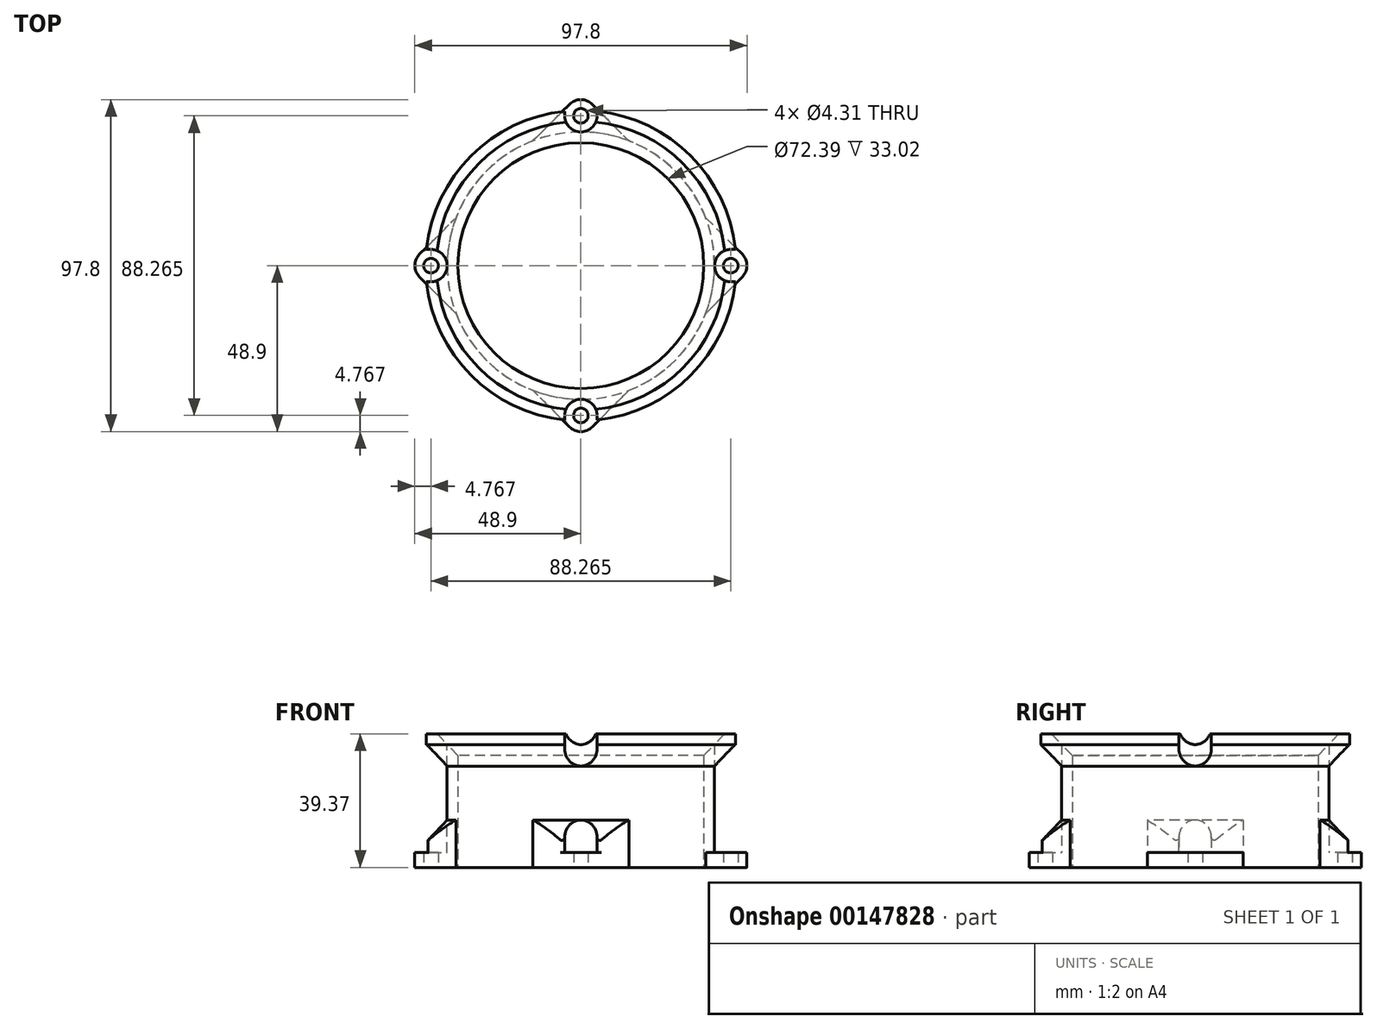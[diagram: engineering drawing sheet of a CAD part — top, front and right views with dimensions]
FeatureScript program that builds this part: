
annotation { "Feature Type Name" : "Feature", "Feature Type Description" : "" }
export const myFeature = defineFeature(function(context is Context, id is Id, definition is map)
    precondition{}
    {
        {
            var Q0;
            Q0=qCreatedBy(makeId("Top.planeOp"),FACE);
            var sketch = newSketch(context, id + "F0", { "sketchPlane" : qUnion([Q0])});
            skCircle(sketch, "E0", {"center": v(0, 0) * mm, "radius": 36.2 * mm});
            skLineSegment(sketch, "E1", {"start": v(-44.13, 0) * mm, "end": v(44.13, 0) * mm, "construction": true});
            skLineSegment(sketch, "E2", {"start": v(0, 44.13) * mm, "end": v(0, -44.13) * mm, "construction": true});
            skArc(sketch, "E3", {"start": v(3.37, 47.5) * mm, "mid": v(0, 48.9) * mm, "end": v(-3.37, 47.5) * mm});
            skLineSegment(sketch, "E4", {"start": v(3.37, 47.5) * mm, "end": v(14.11, 36.75) * mm});
            skArc(sketch, "E5", {"start": v(36.75, 14.11) * mm, "mid": v(27.84, 27.84) * mm, "end": v(14.11, 36.75) * mm});
            skLineSegment(sketch, "E6", {"start": v(-3.37, 47.5) * mm, "end": v(-14.11, 36.75) * mm});
            skArc(sketch, "E7", {"start": v(-47.5, 3.37) * mm, "mid": v(-48.9, 0) * mm, "end": v(-47.5, -3.37) * mm});
            skArc(sketch, "E8", {"start": v(-14.11, 36.75) * mm, "mid": v(-27.84, 27.84) * mm, "end": v(-36.75, 14.11) * mm});
            skArc(sketch, "E9", {"start": v(47.5, -3.37) * mm, "mid": v(48.9, 0) * mm, "end": v(47.5, 3.37) * mm});
            skArc(sketch, "E10", {"start": v(-3.37, -47.5) * mm, "mid": v(0, -48.9) * mm, "end": v(3.37, -47.5) * mm});
            skLineSegment(sketch, "E11", {"start": v(36.75, 14.11) * mm, "end": v(47.5, 3.37) * mm});
            skLineSegment(sketch, "E12", {"start": v(47.5, -3.37) * mm, "end": v(36.75, -14.11) * mm});
            skLineSegment(sketch, "E13", {"start": v(-3.37, -47.5) * mm, "end": v(-14.11, -36.75) * mm});
            skLineSegment(sketch, "E14", {"start": v(3.37, -47.5) * mm, "end": v(14.11, -36.75) * mm});
            skLineSegment(sketch, "E15", {"start": v(-6.74, 44.13) * mm, "end": v(6.74, 44.13) * mm, "construction": true});
            skLineSegment(sketch, "E16", {"start": v(-6.74, -44.13) * mm, "end": v(6.74, -44.13) * mm, "construction": true});
            skLineSegment(sketch, "E17", {"start": v(-47.5, 3.37) * mm, "end": v(-36.75, 14.11) * mm});
            skLineSegment(sketch, "E18", {"start": v(-47.5, -3.37) * mm, "end": v(-36.75, -14.11) * mm});
            skLineSegment(sketch, "E19", {"start": v(44.13, 6.74) * mm, "end": v(44.13, -6.74) * mm, "construction": true});
            skLineSegment(sketch, "E20", {"start": v(-44.13, 6.74) * mm, "end": v(-44.13, -6.74) * mm, "construction": true});
            skArc(sketch, "E21", {"start": v(-36.75, -14.11) * mm, "mid": v(-27.84, -27.84) * mm, "end": v(-14.11, -36.75) * mm});
            skArc(sketch, "E22", {"start": v(14.11, -36.75) * mm, "mid": v(27.84, -27.84) * mm, "end": v(36.75, -14.11) * mm});
            skSolve(sketch);
        }
        {
            var Q0;
            Q0=qSketchRegion(id+"F0",true);
            extrude(context, id + "F1", {"entities" : qUnion([Q0]), "depth" : 4.44 * mm});
        }
        {
            var Q0;
            Q0=makeQuery(id+"F1.opExtrude","CAP_FACE",FACE,{"disambiguationData":[OSD([sQuery(id+"F0.wireOp",EDGE,"E0"),sQuery(id+"F0.wireOp",EDGE,"E3"),sQuery(id+"F0.wireOp",EDGE,"E4"),sQuery(id+"F0.wireOp",EDGE,"E5"),sQuery(id+"F0.wireOp",EDGE,"E6"),sQuery(id+"F0.wireOp",EDGE,"E7"),sQuery(id+"F0.wireOp",EDGE,"E8"),sQuery(id+"F0.wireOp",EDGE,"E9"),sQuery(id+"F0.wireOp",EDGE,"E10"),sQuery(id+"F0.wireOp",EDGE,"E11"),sQuery(id+"F0.wireOp",EDGE,"E12"),sQuery(id+"F0.wireOp",EDGE,"E13"),sQuery(id+"F0.wireOp",EDGE,"E14"),sQuery(id+"F0.wireOp",EDGE,"E17"),sQuery(id+"F0.wireOp",EDGE,"E18"),sQuery(id+"F0.wireOp",EDGE,"E21"),sQuery(id+"F0.wireOp",EDGE,"E22")])],"isStart":false});
            var sketch = newSketch(context, id + "F2", { "sketchPlane" : qUnion([Q0])});
            skCircle(sketch, "E23", {"center": v(0, 0) * mm, "radius": 39.37 * mm});
            skCircle(sketch, "E24", {"center": v(0, 0) * mm, "radius": 36.2 * mm});
            skSolve(sketch);
        }
        {
            var Q0;
            Q0=qSketchRegion(id+"F2",true);
            extrude(context, id + "F3", {"entities" : qUnion([Q0]), "operationType" : NewBodyOperationType.ADD, "depth" : 25.4 * mm});
        }
        {
            var Q0;
            {var subQ3=sQuery(id+"F2.wireOp",EDGE,"E23");var subQ4=sQuery(id+"F0.wireOp",EDGE,"E4");Q0=makeQuery(id+"F3.boolean.opBoolean","SPLIT",EDGE,{"disambiguationData":[TD([makeQuery(id+"F1.opExtrude","SWEPT_FACE",FACE,{"disambiguationData":[OSD([subQ4])]})])],"derivedFrom":makeQuery(id+"F3.opExtrude","CAP_EDGE",EDGE,{"disambiguationData":[OSD([subQ3])],"isStart":true})});}
            var Q1;
            {var subQ0=sQuery(id+"F0.wireOp",EDGE,"E17");var subQ2=sQuery(id+"F2.wireOp",EDGE,"E23");Q1=makeQuery(id+"F3.boolean.opBoolean","SPLIT",EDGE,{"disambiguationData":[TD([makeQuery(id+"F1.opExtrude","SWEPT_FACE",FACE,{"disambiguationData":[OSD([subQ0])]})])],"derivedFrom":makeQuery(id+"F3.opExtrude","CAP_EDGE",EDGE,{"disambiguationData":[OSD([subQ2])],"isStart":true})});}
            var Q2;
            {var subQ0=sQuery(id+"F0.wireOp",EDGE,"E13");var subQ6=sQuery(id+"F2.wireOp",EDGE,"E23");Q2=makeQuery(id+"F3.boolean.opBoolean","SPLIT",EDGE,{"disambiguationData":[TD([makeQuery(id+"F1.opExtrude","SWEPT_FACE",FACE,{"disambiguationData":[OSD([subQ0])]})])],"derivedFrom":makeQuery(id+"F3.opExtrude","CAP_EDGE",EDGE,{"disambiguationData":[OSD([subQ6])],"isStart":true})});}
            var Q3;
            {var subQ0=sQuery(id+"F0.wireOp",EDGE,"E11");var subQ3=sQuery(id+"F2.wireOp",EDGE,"E23");Q3=makeQuery(id+"F3.boolean.opBoolean","SPLIT",EDGE,{"disambiguationData":[TD([makeQuery(id+"F1.opExtrude","SWEPT_FACE",FACE,{"disambiguationData":[OSD([subQ0])]})])],"derivedFrom":makeQuery(id+"F3.opExtrude","CAP_EDGE",EDGE,{"disambiguationData":[OSD([subQ3])],"isStart":true})});}
            chamfer(context, id + "F4", {"entities" : qUnion([Q0, Q1, Q2, Q3]), "width" : 9.52 * mm, "tangentPropagation" : true});
        }
        {
            var Q0;
            Q0=makeQuery(id+"F1.opExtrude","CAP_FACE",FACE,{"disambiguationData":[OSD([sQuery(id+"F0.wireOp",EDGE,"E0"),sQuery(id+"F0.wireOp",EDGE,"E3"),sQuery(id+"F0.wireOp",EDGE,"E4"),sQuery(id+"F0.wireOp",EDGE,"E5"),sQuery(id+"F0.wireOp",EDGE,"E6"),sQuery(id+"F0.wireOp",EDGE,"E7"),sQuery(id+"F0.wireOp",EDGE,"E8"),sQuery(id+"F0.wireOp",EDGE,"E9"),sQuery(id+"F0.wireOp",EDGE,"E10"),sQuery(id+"F0.wireOp",EDGE,"E11"),sQuery(id+"F0.wireOp",EDGE,"E12"),sQuery(id+"F0.wireOp",EDGE,"E13"),sQuery(id+"F0.wireOp",EDGE,"E14"),sQuery(id+"F0.wireOp",EDGE,"E17"),sQuery(id+"F0.wireOp",EDGE,"E18"),sQuery(id+"F0.wireOp",EDGE,"E21"),sQuery(id+"F0.wireOp",EDGE,"E22")])],"isStart":true});
            cPlane(context, id + "F5", {"entities" : qUnion([Q0]), "cplaneType" : CPlaneType.OFFSET, "offset" : 4.44 * mm, "oppositeDirection" : true, "width" : 152.4 * mm, "height" : 152.4 * mm});
        }
        {
            var Q0;
            Q0=makeQuery(id+"F3.opExtrude","CAP_FACE",FACE,{"disambiguationData":[OSD([sQuery(id+"F2.wireOp",EDGE,"E23"),sQuery(id+"F2.wireOp",EDGE,"E24")])],"isStart":false});
            var sketch = newSketch(context, id + "F6", { "sketchPlane" : qUnion([Q0])});
            skCircle(sketch, "E25", {"center": v(0, 0) * mm, "radius": 36.2 * mm});
            skCircle(sketch, "E26", {"center": v(0, 0) * mm, "radius": 45.72 * mm});
            skSolve(sketch);
        }
        {
            var Q0;
            Q0=qSketchRegion(id+"F6",true);
            extrude(context, id + "F7", {"entities" : qUnion([Q0]), "operationType" : NewBodyOperationType.ADD, "depth" : 9.52 * mm});
        }
        {
            var Q0;
            Q0=qCreatedBy(id+"F5.planeOp",FACE);
            var sketch = newSketch(context, id + "F8", { "sketchPlane" : qUnion([Q0])});
            skLineSegment(sketch, "E27.bottom", {"start": v(4.76, 39.37) * mm, "end": v(-4.76, 39.37) * mm});
            skLineSegment(sketch, "E27.top", {"start": v(4.76, 48.9) * mm, "end": v(-4.76, 48.9) * mm});
            skLineSegment(sketch, "E27.left", {"start": v(4.76, 39.37) * mm, "end": v(4.76, 48.9) * mm});
            skLineSegment(sketch, "E27.right", {"start": v(-4.76, 39.37) * mm, "end": v(-4.76, 48.9) * mm});
            skPoint(sketch, "E27.middle", {"position": v(0, 44.13) * mm});
            skLineSegment(sketch, "E28.bottom", {"start": v(48.9, -4.76) * mm, "end": v(39.37, -4.76) * mm});
            skLineSegment(sketch, "E28.top", {"start": v(48.9, 4.76) * mm, "end": v(39.37, 4.76) * mm});
            skLineSegment(sketch, "E28.left", {"start": v(48.9, -4.76) * mm, "end": v(48.9, 4.76) * mm});
            skLineSegment(sketch, "E28.right", {"start": v(39.37, -4.76) * mm, "end": v(39.37, 4.76) * mm});
            skPoint(sketch, "E28.middle", {"position": v(44.13, 0) * mm});
            skLineSegment(sketch, "E29.bottom", {"start": v(-4.76, -48.9) * mm, "end": v(4.76, -48.9) * mm});
            skLineSegment(sketch, "E29.top", {"start": v(-4.76, -39.37) * mm, "end": v(4.76, -39.37) * mm});
            skLineSegment(sketch, "E29.left", {"start": v(-4.76, -48.9) * mm, "end": v(-4.76, -39.37) * mm});
            skLineSegment(sketch, "E29.right", {"start": v(4.76, -48.9) * mm, "end": v(4.76, -39.37) * mm});
            skPoint(sketch, "E29.middle", {"position": v(0, -44.13) * mm});
            skLineSegment(sketch, "E30.bottom", {"start": v(-48.9, 4.76) * mm, "end": v(-39.37, 4.76) * mm});
            skLineSegment(sketch, "E30.top", {"start": v(-48.9, -4.76) * mm, "end": v(-39.37, -4.76) * mm});
            skLineSegment(sketch, "E30.left", {"start": v(-48.9, 4.76) * mm, "end": v(-48.9, -4.76) * mm});
            skLineSegment(sketch, "E30.right", {"start": v(-39.37, 4.76) * mm, "end": v(-39.37, -4.76) * mm});
            skPoint(sketch, "E30.middle", {"position": v(-44.13, 0) * mm});
            skSolve(sketch);
        }
        {
            var Q0;
            Q0=qSketchRegion(id+"F8",true);
            var Q1;
            Q1=makeQuery(id+"F7.opExtrude","CAP_FACE",FACE,{"disambiguationData":[OSD([sQuery(id+"F6.wireOp",EDGE,"E25"),sQuery(id+"F6.wireOp",EDGE,"E26")])],"isStart":false});
            extrude(context, id + "F9", {"entities" : qUnion([Q0]), "operationType" : NewBodyOperationType.REMOVE, "endBound" : BoundingType.UP_TO_SURFACE, "oppositeDirection" : true, "endBoundEntityFace" : qUnion([Q1]), "depth" : 25.4 * mm});
        }
        {
            var Q0;
            Q0=makeQuery(id+"F9.boolean.opBoolean","COPY",EDGE,{"derivedFrom":makeQuery(id+"F9.opExtrude","SWEPT_EDGE",EDGE,{"disambiguationData":[OSD([sQuery(id+"F8.wireOp",EDGE,"E29.top"),sQuery(id+"F8.wireOp",EDGE,"E29.right")])]})});
            var Q1;
            Q1=makeQuery(id+"F9.boolean.opBoolean","COPY",EDGE,{"derivedFrom":makeQuery(id+"F9.opExtrude","SWEPT_EDGE",EDGE,{"disambiguationData":[OSD([sQuery(id+"F8.wireOp",EDGE,"E29.top"),sQuery(id+"F8.wireOp",EDGE,"E29.left")])]})});
            var Q2;
            Q2=makeQuery(id+"F9.boolean.opBoolean","COPY",EDGE,{"derivedFrom":makeQuery(id+"F9.opExtrude","SWEPT_EDGE",EDGE,{"disambiguationData":[OSD([sQuery(id+"F8.wireOp",EDGE,"E30.bottom"),sQuery(id+"F8.wireOp",EDGE,"E30.right")])]})});
            var Q3;
            Q3=makeQuery(id+"F9.boolean.opBoolean","COPY",EDGE,{"derivedFrom":makeQuery(id+"F9.opExtrude","SWEPT_EDGE",EDGE,{"disambiguationData":[OSD([sQuery(id+"F8.wireOp",EDGE,"E30.top"),sQuery(id+"F8.wireOp",EDGE,"E30.right")])]})});
            var Q4;
            Q4=makeQuery(id+"F9.boolean.opBoolean","COPY",EDGE,{"derivedFrom":makeQuery(id+"F9.opExtrude","SWEPT_EDGE",EDGE,{"disambiguationData":[OSD([sQuery(id+"F8.wireOp",EDGE,"E27.bottom"),sQuery(id+"F8.wireOp",EDGE,"E27.left")])]})});
            var Q5;
            Q5=makeQuery(id+"F9.boolean.opBoolean","COPY",EDGE,{"derivedFrom":makeQuery(id+"F9.opExtrude","SWEPT_EDGE",EDGE,{"disambiguationData":[OSD([sQuery(id+"F8.wireOp",EDGE,"E27.bottom"),sQuery(id+"F8.wireOp",EDGE,"E27.right")])]})});
            var Q6;
            Q6=makeQuery(id+"F9.boolean.opBoolean","COPY",EDGE,{"derivedFrom":makeQuery(id+"F9.opExtrude","SWEPT_EDGE",EDGE,{"disambiguationData":[OSD([sQuery(id+"F8.wireOp",EDGE,"E28.top"),sQuery(id+"F8.wireOp",EDGE,"E28.right")])]})});
            var Q7;
            Q7=makeQuery(id+"F9.boolean.opBoolean","COPY",EDGE,{"derivedFrom":makeQuery(id+"F9.opExtrude","SWEPT_EDGE",EDGE,{"disambiguationData":[OSD([sQuery(id+"F8.wireOp",EDGE,"E28.bottom"),sQuery(id+"F8.wireOp",EDGE,"E28.right")])]})});
            fillet(context, id + "F10", {"entities" : qUnion([Q0, Q1, Q2, Q3, Q4, Q5, Q6, Q7]), "radius" : 4.76 * mm, "tangentPropagation" : true, "allowEdgeOverflow" : false});
        }
        {
            var Q0;
            Q0=makeQuery(id+"F9.boolean.opBoolean","INTERSECT",EDGE,{"derivedFrom":[makeQuery(id+"F1.opExtrude","SWEPT_FACE",FACE,{"disambiguationData":[OSD([sQuery(id+"F0.wireOp",EDGE,"E13")])]}),makeQuery(id+"F9.opExtrude","SWEPT_FACE",FACE,{"disambiguationData":[OSD([sQuery(id+"F8.wireOp",EDGE,"E27.right")])]})]});
            var Q1;
            Q1=makeQuery(id+"F9.boolean.opBoolean","INTERSECT",EDGE,{"derivedFrom":[makeQuery(id+"F1.opExtrude","SWEPT_FACE",FACE,{"disambiguationData":[OSD([sQuery(id+"F0.wireOp",EDGE,"E14")])]}),makeQuery(id+"F9.opExtrude","SWEPT_FACE",FACE,{"disambiguationData":[OSD([sQuery(id+"F8.wireOp",EDGE,"E27.left")])]})]});
            var Q2;
            Q2=makeQuery(id+"F9.boolean.opBoolean","INTERSECT",EDGE,{"derivedFrom":[makeQuery(id+"F1.opExtrude","SWEPT_FACE",FACE,{"disambiguationData":[OSD([sQuery(id+"F0.wireOp",EDGE,"E11")])]}),makeQuery(id+"F9.opExtrude","SWEPT_FACE",FACE,{"disambiguationData":[OSD([sQuery(id+"F8.wireOp",EDGE,"E28.bottom")])]})]});
            var Q3;
            Q3=makeQuery(id+"F9.boolean.opBoolean","INTERSECT",EDGE,{"derivedFrom":[makeQuery(id+"F1.opExtrude","SWEPT_FACE",FACE,{"disambiguationData":[OSD([sQuery(id+"F0.wireOp",EDGE,"E12")])]}),makeQuery(id+"F9.opExtrude","SWEPT_FACE",FACE,{"disambiguationData":[OSD([sQuery(id+"F8.wireOp",EDGE,"E28.top")])]})]});
            var Q4;
            Q4=makeQuery(id+"F9.boolean.opBoolean","INTERSECT",EDGE,{"derivedFrom":[makeQuery(id+"F1.opExtrude","SWEPT_FACE",FACE,{"disambiguationData":[OSD([sQuery(id+"F0.wireOp",EDGE,"E4")])]}),makeQuery(id+"F9.opExtrude","SWEPT_FACE",FACE,{"disambiguationData":[OSD([sQuery(id+"F8.wireOp",EDGE,"E29.right")])]})]});
            var Q5;
            Q5=makeQuery(id+"F9.boolean.opBoolean","INTERSECT",EDGE,{"derivedFrom":[makeQuery(id+"F1.opExtrude","SWEPT_FACE",FACE,{"disambiguationData":[OSD([sQuery(id+"F0.wireOp",EDGE,"E6")])]}),makeQuery(id+"F9.opExtrude","SWEPT_FACE",FACE,{"disambiguationData":[OSD([sQuery(id+"F8.wireOp",EDGE,"E29.left")])]})]});
            var Q6;
            Q6=makeQuery(id+"F9.boolean.opBoolean","INTERSECT",EDGE,{"derivedFrom":[makeQuery(id+"F1.opExtrude","SWEPT_FACE",FACE,{"disambiguationData":[OSD([sQuery(id+"F0.wireOp",EDGE,"E18")])]}),makeQuery(id+"F9.opExtrude","SWEPT_FACE",FACE,{"disambiguationData":[OSD([sQuery(id+"F8.wireOp",EDGE,"E30.bottom")])]})]});
            var Q7;
            Q7=makeQuery(id+"F9.boolean.opBoolean","INTERSECT",EDGE,{"derivedFrom":[makeQuery(id+"F1.opExtrude","SWEPT_FACE",FACE,{"disambiguationData":[OSD([sQuery(id+"F0.wireOp",EDGE,"E17")])]}),makeQuery(id+"F9.opExtrude","SWEPT_FACE",FACE,{"disambiguationData":[OSD([sQuery(id+"F8.wireOp",EDGE,"E30.top")])]})]});
            fillet(context, id + "F11", {"entities" : qUnion([Q0, Q1, Q2, Q3, Q4, Q5, Q6, Q7]), "radius" : 0.76 * mm, "tangentPropagation" : true, "allowEdgeOverflow" : false});
        }
        {
            var Q0;
            Q0=makeQuery(id+"F1.opExtrude","CAP_FACE",FACE,{"disambiguationData":[OSD([sQuery(id+"F0.wireOp",EDGE,"E0"),sQuery(id+"F0.wireOp",EDGE,"E3"),sQuery(id+"F0.wireOp",EDGE,"E4"),sQuery(id+"F0.wireOp",EDGE,"E5"),sQuery(id+"F0.wireOp",EDGE,"E6"),sQuery(id+"F0.wireOp",EDGE,"E7"),sQuery(id+"F0.wireOp",EDGE,"E8"),sQuery(id+"F0.wireOp",EDGE,"E9"),sQuery(id+"F0.wireOp",EDGE,"E10"),sQuery(id+"F0.wireOp",EDGE,"E11"),sQuery(id+"F0.wireOp",EDGE,"E12"),sQuery(id+"F0.wireOp",EDGE,"E13"),sQuery(id+"F0.wireOp",EDGE,"E14"),sQuery(id+"F0.wireOp",EDGE,"E17"),sQuery(id+"F0.wireOp",EDGE,"E18"),sQuery(id+"F0.wireOp",EDGE,"E21"),sQuery(id+"F0.wireOp",EDGE,"E22")])],"isStart":true});
            var sketch = newSketch(context, id + "F12", { "sketchPlane" : qUnion([Q0])});
            skCircle(sketch, "E31", {"center": v(-44.13, 0) * mm, "radius": 2.15 * mm});
            skCircle(sketch, "E32", {"center": v(0, 44.13) * mm, "radius": 2.15 * mm});
            skCircle(sketch, "E33", {"center": v(44.13, 0) * mm, "radius": 2.15 * mm});
            skCircle(sketch, "E34", {"center": v(0, -44.13) * mm, "radius": 2.15 * mm});
            skSolve(sketch);
        }
        {
            var Q0;
            Q0=qSketchRegion(id+"F12",true);
            var Q1;
            Q1=makeQuery(id+"F9.boolean.opBoolean","COPY",FACE,{"derivedFrom":makeQuery(id+"F9.opExtrude","CAP_FACE",FACE,{"disambiguationData":[OSD([sQuery(id+"F8.wireOp",EDGE,"E30.bottom"),sQuery(id+"F8.wireOp",EDGE,"E30.top"),sQuery(id+"F8.wireOp",EDGE,"E30.left"),sQuery(id+"F8.wireOp",EDGE,"E30.right")])],"isStart":true})});
            extrude(context, id + "F13", {"entities" : qUnion([Q0]), "operationType" : NewBodyOperationType.REMOVE, "endBound" : BoundingType.UP_TO_SURFACE, "oppositeDirection" : true, "endBoundEntityFace" : qUnion([Q1]), "depth" : 25.4 * mm});
        }
        {
            var Q0;
            Q0=makeQuery(id+"F7.opExtrude","CAP_EDGE",EDGE,{"disambiguationData":[OSD([sQuery(id+"F6.wireOp",EDGE,"E25")])],"isStart":false});
            var Q1;
            Q1=makeQuery(id+"F7.opExtrude","CAP_EDGE",EDGE,{"disambiguationData":[OSD([sQuery(id+"F6.wireOp",EDGE,"E26")])],"isStart":true});
            chamfer(context, id + "F14", {"entities" : qUnion([Q0, Q1]), "width" : 6.35 * mm, "tangentPropagation" : true});
        }
    });
